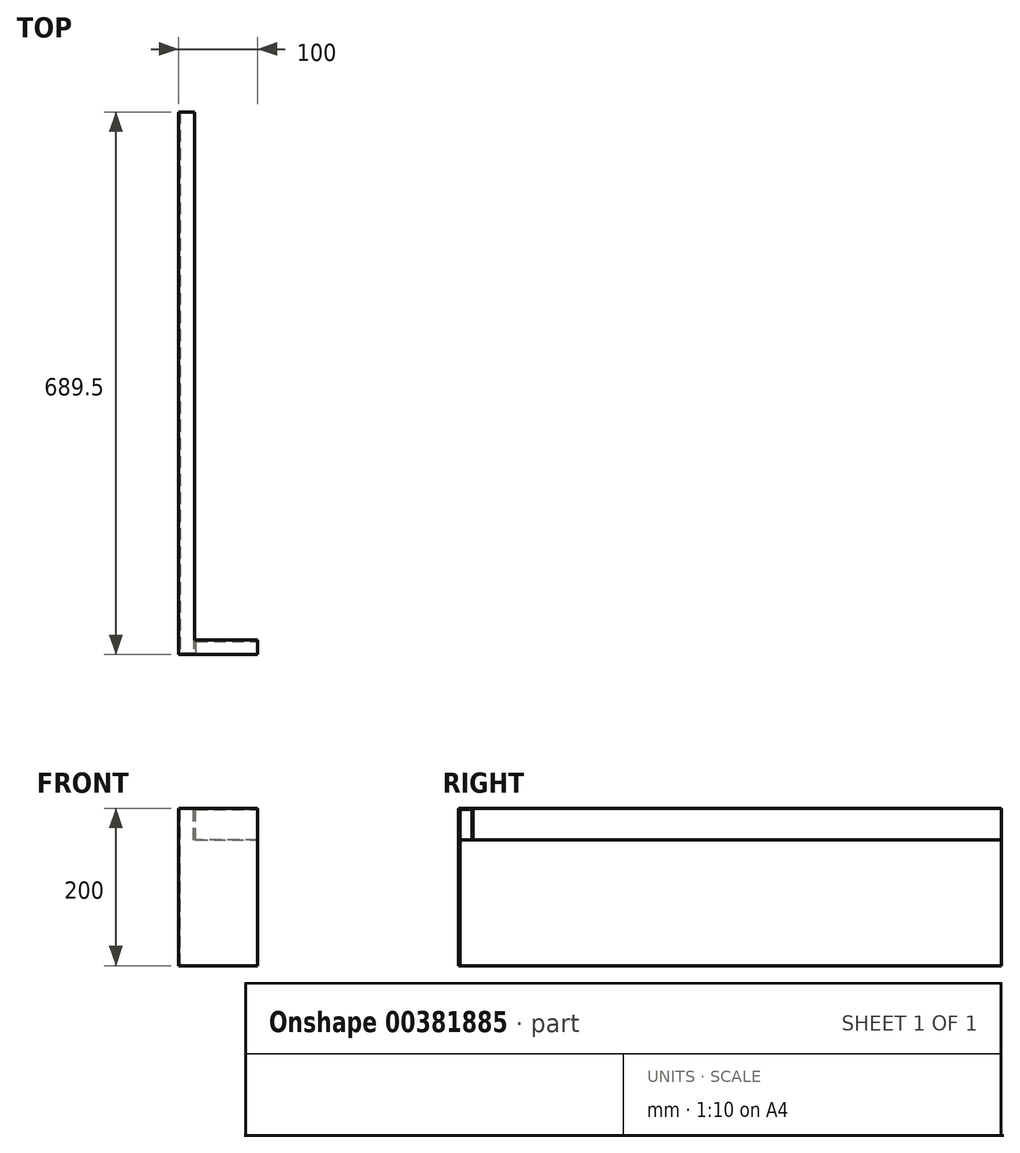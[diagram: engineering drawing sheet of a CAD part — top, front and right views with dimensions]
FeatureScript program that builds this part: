
annotation { "Feature Type Name" : "Feature", "Feature Type Description" : "" }
export const myFeature = defineFeature(function(context is Context, id is Id, definition is map)
    precondition{}
    {
        {
            var Q0;
            Q0=qCreatedBy(makeId("Front.planeOp"),FACE);
            var sketch = newSketch(context, id + "F0", { "sketchPlane" : qUnion([Q0])});
            skLineSegment(sketch, "E0.bottom", {"start": v(10, -100) * mm, "end": v(-10, -100) * mm});
            skLineSegment(sketch, "E0.top", {"start": v(10, 100) * mm, "end": v(-10, 100) * mm});
            skLineSegment(sketch, "E0.left", {"start": v(10, -100) * mm, "end": v(10, 100) * mm});
            skLineSegment(sketch, "E0.right", {"start": v(-10, -100) * mm, "end": v(-10, 100) * mm});
            skPoint(sketch, "E0.middle", {"position": v(0, 0) * mm});
            skSolve(sketch);
        }
        {
            var Q0;
            Q0 = qSketchRegion(id + "F0", true);
            extrude(context, id + "F1", {"entities" : qUnion([Q0]), "depth" : 688 * mm});
        }
        {
            var Q0;
            Q0=makeQuery(id+"F1.opExtrude","CAP_FACE",FACE,{"disambiguationData":[OSD([sQuery(id+"F0.wireOp",EDGE,"E0.bottom"),sQuery(id+"F0.wireOp",EDGE,"E0.top"),sQuery(id+"F0.wireOp",EDGE,"E0.left"),sQuery(id+"F0.wireOp",EDGE,"E0.right")])],"isStart":false});
            var sketch = newSketch(context, id + "F2", { "sketchPlane" : qUnion([Q0])});
            skPoint(sketch, "E1.oppositeSnap0", {"position": v(0, 100) * mm});
            skLineSegment(sketch, "E1.bottom", {"start": v(10, -100) * mm, "end": v(-8.5, -100) * mm});
            skLineSegment(sketch, "E1.top", {"start": v(10, 60) * mm, "end": v(-8.5, 60) * mm});
            skLineSegment(sketch, "E1.left", {"start": v(10, -100) * mm, "end": v(10, 60) * mm});
            skLineSegment(sketch, "E1.right", {"start": v(-8.5, -100) * mm, "end": v(-8.5, 60) * mm});
            skSolve(sketch);
        }
        {
            var Q0;
            Q0 = qSketchRegion(id + "F2", true);
            extrude(context, id + "F3", {"entities" : qUnion([Q0]), "operationType" : NewBodyOperationType.REMOVE, "oppositeDirection" : true, "depth" : 688 * mm});
        }
        {
            var Q0;
            Q0=makeQuery(id+"F1.opExtrude","CAP_FACE",FACE,{"disambiguationData":[OSD([sQuery(id+"F0.wireOp",EDGE,"E0.bottom"),sQuery(id+"F0.wireOp",EDGE,"E0.top"),sQuery(id+"F0.wireOp",EDGE,"E0.left"),sQuery(id+"F0.wireOp",EDGE,"E0.right")])],"isStart":false});
            var sketch = newSketch(context, id + "F4", { "sketchPlane" : qUnion([Q0])});
            skLineSegment(sketch, "E2.bottom", {"start": v(8.5, 60) * mm, "end": v(-8.5, 60) * mm});
            skLineSegment(sketch, "E2.top", {"start": v(8.5, 98.5) * mm, "end": v(-8.5, 98.5) * mm});
            skLineSegment(sketch, "E2.left", {"start": v(8.5, 60) * mm, "end": v(8.5, 98.5) * mm});
            skLineSegment(sketch, "E2.right", {"start": v(-8.5, 60) * mm, "end": v(-8.5, 98.5) * mm});
            skSolve(sketch);
        }
        {
            var Q0;
            Q0=makeQuery(id+"F4.imprint","IMPRINT",FACE,{"disambiguationData":[TD([[makeQuery(id+"F4.imprint","IMPRINT",EDGE,{"derivedFrom":sQuery(id+"F4.wireOp",EDGE,"E2.bottom")}),-1.0]])]});
            extrude(context, id + "F5", {"entities" : qUnion([Q0]), "operationType" : NewBodyOperationType.REMOVE, "oppositeDirection" : true, "depth" : 688 * mm});
        }
        {
            var Q0;
            Q0=makeQuery(id+"F1.opExtrude","CAP_FACE",FACE,{"disambiguationData":[OSD([sQuery(id+"F0.wireOp",EDGE,"E0.bottom"),sQuery(id+"F0.wireOp",EDGE,"E0.top"),sQuery(id+"F0.wireOp",EDGE,"E0.left"),sQuery(id+"F0.wireOp",EDGE,"E0.right")])],"isStart":false});
            var sketch = newSketch(context, id + "F6", { "sketchPlane" : qUnion([Q0])});
            skLineSegment(sketch, "E3.bottom", {"start": v(-10, -100) * mm, "end": v(90, -100) * mm});
            skLineSegment(sketch, "E3.top", {"start": v(-10, 100) * mm, "end": v(90, 100) * mm});
            skLineSegment(sketch, "E3.left", {"start": v(-10, -100) * mm, "end": v(-10, 100) * mm});
            skLineSegment(sketch, "E3.right", {"start": v(90, -100) * mm, "end": v(90, 100) * mm});
            skSolve(sketch);
        }
        {
            var Q0;
            Q0 = qSketchRegion(id + "F6", true);
            extrude(context, id + "F7", {"entities" : qUnion([Q0]), "operationType" : NewBodyOperationType.ADD, "depth" : 1.5 * mm});
        }
        {
            var Q0;
            Q0=makeQuery(id+"F1.opExtrude","SWEPT_FACE",FACE,{"disambiguationData":[OSD([sQuery(id+"F0.wireOp",EDGE,"E0.left")])]});
            var sketch = newSketch(context, id + "F8", { "sketchPlane" : qUnion([Q0])});
            skLineSegment(sketch, "E4.bottom", {"start": v(-688, 100) * mm, "end": v(-671, 100) * mm});
            skLineSegment(sketch, "E4.top", {"start": v(-688, 60) * mm, "end": v(-671, 60) * mm});
            skLineSegment(sketch, "E4.left", {"start": v(-688, 100) * mm, "end": v(-688, 60) * mm});
            skLineSegment(sketch, "E4.right", {"start": v(-671, 100) * mm, "end": v(-671, 60) * mm});
            skSolve(sketch);
        }
        {
            var Q0;
            Q0 = qSketchRegion(id + "F8", true);
            extrude(context, id + "F9", {"entities" : qUnion([Q0]), "operationType" : NewBodyOperationType.ADD, "depth" : 80 * mm});
        }
        {
            var Q0;
            Q0=makeQuery(id+"F9.boolean.opBoolean","MERGE",FACE,{"derivedFrom":[makeQuery(id+"F7.opExtrude","SWEPT_FACE",FACE,{"disambiguationData":[OSD([sQuery(id+"F6.wireOp",EDGE,"E3.right")])]}),makeQuery(id+"F9.opExtrude","CAP_FACE",FACE,{"disambiguationData":[OSD([sQuery(id+"F8.wireOp",EDGE,"E4.bottom"),sQuery(id+"F8.wireOp",EDGE,"E4.top"),sQuery(id+"F8.wireOp",EDGE,"E4.left"),sQuery(id+"F8.wireOp",EDGE,"E4.right")])],"isStart":false})]});
            var sketch = newSketch(context, id + "F10", { "sketchPlane" : qUnion([Q0])});
            skLineSegment(sketch, "E5.bottom", {"start": v(-672.5, 60) * mm, "end": v(-688, 60) * mm});
            skLineSegment(sketch, "E5.top", {"start": v(-672.5, 98.5) * mm, "end": v(-688, 98.5) * mm});
            skLineSegment(sketch, "E5.left", {"start": v(-672.5, 60) * mm, "end": v(-672.5, 98.5) * mm});
            skLineSegment(sketch, "E5.right", {"start": v(-688, 60) * mm, "end": v(-688, 98.5) * mm});
            skSolve(sketch);
        }
        {
            var Q0;
            Q0 = qSketchRegion(id + "F10", true);
            extrude(context, id + "F11", {"entities" : qUnion([Q0]), "operationType" : NewBodyOperationType.REMOVE, "oppositeDirection" : true, "depth" : 78.5 * mm});
        }
    });
